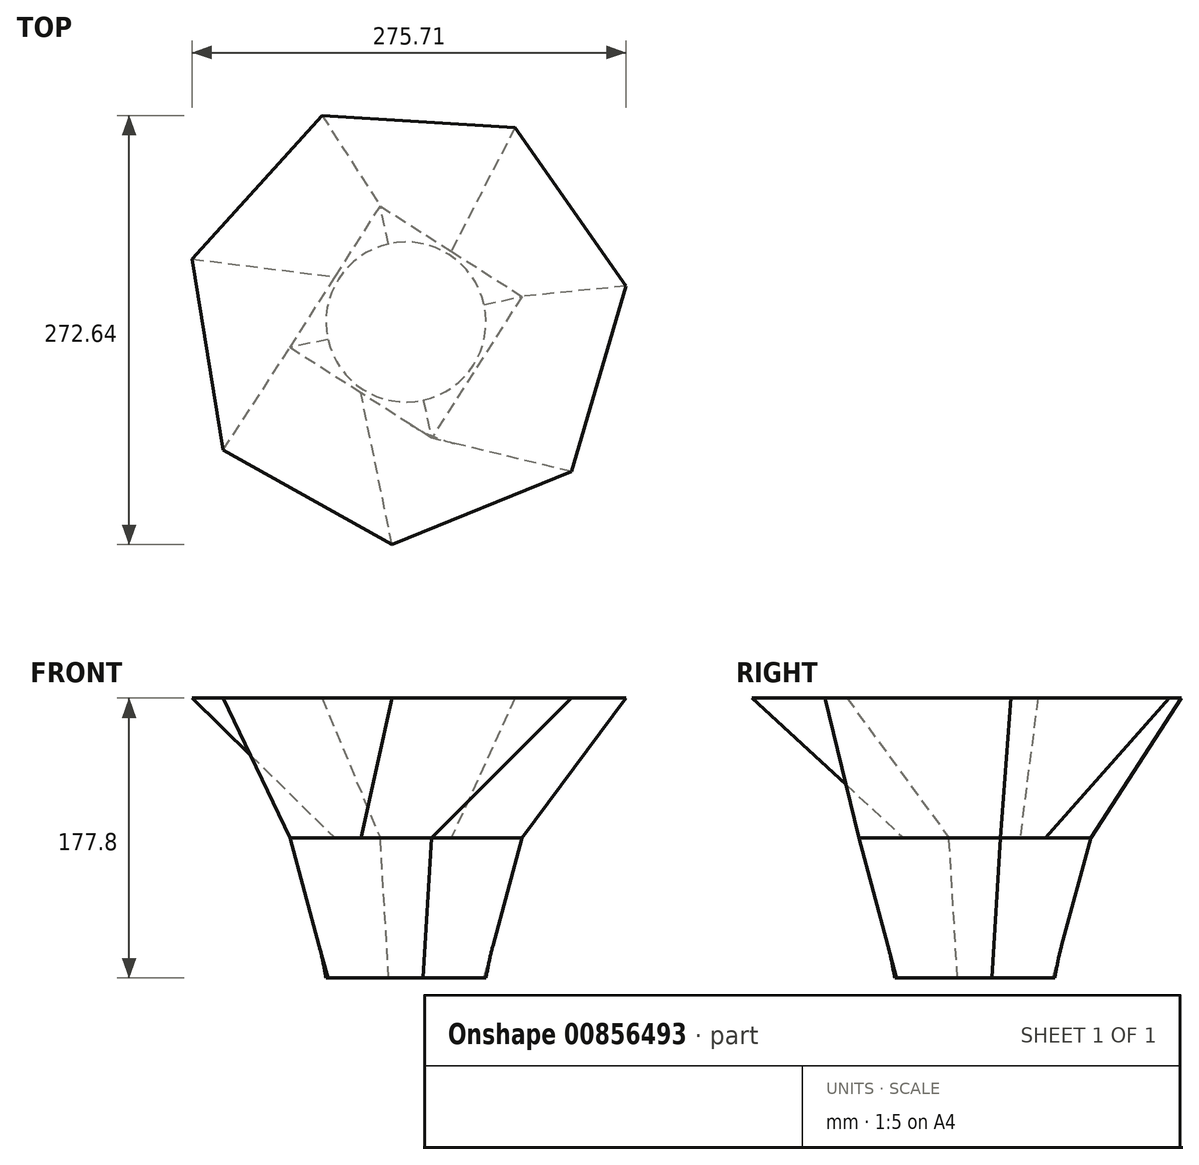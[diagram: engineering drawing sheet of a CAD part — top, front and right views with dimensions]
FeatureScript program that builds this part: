
annotation { "Feature Type Name" : "Feature", "Feature Type Description" : "" }
export const myFeature = defineFeature(function(context is Context, id is Id, definition is map)
    precondition{}
    {
        {
            var Q0;
            Q0=qCreatedBy(makeId("Top.planeOp"),FACE);
            cPlane(context, id + "F0", {"entities" : qUnion([Q0]), "cplaneType" : CPlaneType.OFFSET, "offset" : 88.9 * mm, "width" : 152.4 * mm, "height" : 152.4 * mm});
        }
        {
            var Q0;
            Q0=qCreatedBy(id+"F0.planeOp",FACE);
            cPlane(context, id + "F1", {"entities" : qUnion([Q0]), "cplaneType" : CPlaneType.OFFSET, "offset" : 88.9 * mm, "width" : 152.4 * mm, "height" : 152.4 * mm});
        }
        {
            var Q0;
            Q0=qCreatedBy(makeId("Top.planeOp"),FACE);
            var sketch = newSketch(context, id + "F2", { "sketchPlane" : qUnion([Q0])});
            skCircle(sketch, "E0", {"center": v(0, 0) * mm, "radius": 50.8 * mm});
            skSolve(sketch);
        }
        {
            var Q0;
            Q0=qCreatedBy(id+"F0.planeOp",FACE);
            var sketch = newSketch(context, id + "F3", { "sketchPlane" : qUnion([Q0])});
            skCircle(sketch, "E1.cCircle", {"center": v(0, 0) * mm, "radius": 53.36 * mm, "construction": true});
            skLineSegment(sketch, "E1.0", {"start": v(-16.3, 73.67) * mm, "end": v(73.67, 16.3) * mm});
            skLineSegment(sketch, "E1.1", {"start": v(73.67, 16.3) * mm, "end": v(16.3, -73.67) * mm});
            skLineSegment(sketch, "E1.2", {"start": v(16.3, -73.67) * mm, "end": v(-73.67, -16.3) * mm});
            skLineSegment(sketch, "E1.3", {"start": v(-73.67, -16.3) * mm, "end": v(-16.3, 73.67) * mm});
            skPoint(sketch, "E1.0.midPoint", {"position": v(28.68, 45) * mm});
            skSolve(sketch);
        }
        {
            var Q0;
            Q0=makeQuery(id+"F2.imprint","IMPRINT",FACE,{"disambiguationData":[TD([[makeQuery(id+"F2.imprint","IMPRINT",EDGE,{"derivedFrom":sQuery(id+"F2.wireOp",EDGE,"E0")}),1.0]])]});
            var Q1;
            Q1=makeQuery(id+"F3.imprint","IMPRINT",FACE,{"disambiguationData":[TD([[makeQuery(id+"F3.imprint","IMPRINT",EDGE,{"derivedFrom":sQuery(id+"F3.wireOp",EDGE,"E1.0")}),-1.0]])]});
            loft(context, id + "F4", {"sheetProfilesArray" : [{ "sheetProfileEntities" : qUnion([Q0]) }, { "sheetProfileEntities" : qUnion([Q1]) }]});
        }
        {
            var Q0;
            Q0=qCreatedBy(id+"F1.planeOp",FACE);
            var sketch = newSketch(context, id + "F5", { "sketchPlane" : qUnion([Q0])});
            skCircle(sketch, "E2.cCircle", {"center": v(0, 0) * mm, "radius": 127.65 * mm, "construction": true});
            skLineSegment(sketch, "E2.0", {"start": v(-53.37, 131.24) * mm, "end": v(69.33, 123.55) * mm});
            skLineSegment(sketch, "E2.1", {"start": v(69.33, 123.55) * mm, "end": v(139.83, 22.83) * mm});
            skLineSegment(sketch, "E2.2", {"start": v(139.83, 22.83) * mm, "end": v(105.03, -95.09) * mm});
            skLineSegment(sketch, "E2.3", {"start": v(105.03, -95.09) * mm, "end": v(-8.86, -141.4) * mm});
            skLineSegment(sketch, "E2.4", {"start": v(-8.86, -141.4) * mm, "end": v(-116.07, -81.24) * mm});
            skLineSegment(sketch, "E2.5", {"start": v(-116.07, -81.24) * mm, "end": v(-135.88, 40.1) * mm});
            skLineSegment(sketch, "E2.6", {"start": v(-135.88, 40.1) * mm, "end": v(-53.37, 131.24) * mm});
            skPoint(sketch, "E2.0.midPoint", {"position": v(7.98, 127.4) * mm});
            skSolve(sketch);
        }
        {
            var Q1;
            Q1=makeQuery(id+"F5.imprint","IMPRINT",FACE,{"disambiguationData":[TD([[makeQuery(id+"F5.imprint","IMPRINT",EDGE,{"derivedFrom":sQuery(id+"F5.wireOp",EDGE,"E2.0")}),-1.0]])]});
            var Q2;
            Q2=makeQuery(id+"F4.opLoft","CAP_FACE",FACE,{"disambiguationData":[OSD([makeQuery(id+"F3.imprint","IMPRINT",FACE,{"disambiguationData":[TD([[makeQuery(id+"F3.imprint","IMPRINT",EDGE,{"derivedFrom":sQuery(id+"F3.wireOp",EDGE,"E1.0")}),-1.0]])]})])],"isStart":true});
            loft(context, id + "F6", {"operationType" : NewBodyOperationType.ADD, "sheetProfilesArray" : [{ "sheetProfileEntities" : qUnion([Q1]) }, { "sheetProfileEntities" : qUnion([Q2]) }]});
        }
    });
